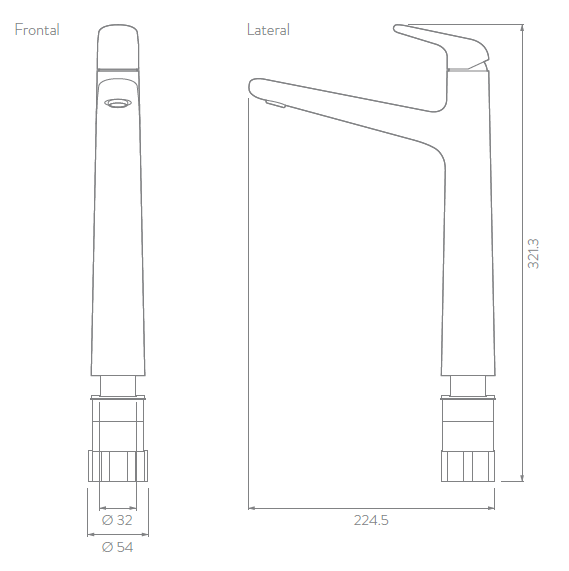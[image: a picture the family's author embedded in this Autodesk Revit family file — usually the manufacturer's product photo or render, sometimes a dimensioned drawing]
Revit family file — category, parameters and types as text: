
# Revit family: KR1195551_Grifería Lavamanos Monocontrol Koral Alta Niquel
name_source: partatom
category: Plumbing Fixtures
units: mm (PartAtom-declared; Revit-internal decimal feet)

## family parameters
Always vertical = Yes
Cut with Voids When Loaded = No
OmniClass Number = 23.31.11.00
OmniClass Title = Faucets
Part Type = Normal
Room Calculation Point = No
Round Connector Dimension = Use Diameter
Shared = No
Work Plane-Based = No

## types (1)
- KR1195551_Grifería Lavamanos Monocontrol Koral Alta Niquel
    Acabado = Corona_Niquel
    Alto = 192 mm  [stored 0.629921 ft]
    Altura de la grifería = Media
    Ancho = 54 mm  [stored 0.177165 ft]
    Capacidad de flujo = 60 psi: 4,86 L/min.
    Colección = Liquid
    Consumo de agua = 5.7 lt
    Creado por = IDD
    Description = La línea de griferías, duchas y accesorios Liquid se inspira en la tensión superficial del agua y en cómo esta crea formas armoniosas adaptándose al ambiente. Al igual que el agua, las superficies de las griferías Liquid juegan con la luz y los reflejos que fluyen alrededorde sus formas, sus líneas continuas y simplicidad formal proporcionan la ventaja práctica y limpieza sin esfuerzo.
Incluye la tecnología Ecostream, de ahorro de agua; y la tecnología ThermoControl, de control más preciso de la temperatura.
Incluye apertura con accionamiento central en frío que evita el encendido automático de calentadores y calderas ahorrando energía; además, es de fácil limpieza gracias al diseño que evita la acumulación de impurezas, es resistente a la corrosión, pelado y decoloración por agua y tiene recubrimientos no tóxicos.
    Fecha de creación = 09/10/2020
    Garantía = 30 años en estructura
    Garantías de otros componentes = 5 años en acabados
    Incluye = Cuerpo, Manija
    Linea = Liquid
    Longitud = 181 mm  [stored 0.593832 ft]
    Material = Metálico
    Peso  Bruto = 1.480 g. - 3,26 lb.
    Peso neto = 1.320 g. - 2,91 lb.
    Presión máxima recomendada = 125 psi (860 Kpa)
    Presión mínima recomendada = 20 psi (140 Kpa)
    Productos compatibles = Lavamanos de mesón integrado, Lavamanos para sobreponer, Lavamanos para incrustar
Lavamanos de pedestal, Lavamanos de semipedestal,Lavamanos de colgar
    Resistencia = Resistente a la corrosión pelado y decoloración por agua
    Sistema de accionamiento = Palanca monocontrol
    Tecnologías = DuraCrome EcoStream ThermoControl
    Temperaturas máxima de trabajo = 71°C / 159,8°F
    Temperaturas mínima de trabajo = 5°C / 41 °F
    Tipo de Chorro = Espumoso
    Tipo de Grifería = Monocontrol
    Tipo de manija/accionamiento = Palanca
    URL = https://corona.co
    Uso = Residencial
    Vida útil = 500.000 ciclos.

note: [stored X ft] marks values corroborated as IEEE doubles in the binary element streams (Revit-internal decimal feet)

## geometry (parser evidence)
native form markers: Sweep x8
no freeform markers — native parametric forms only
